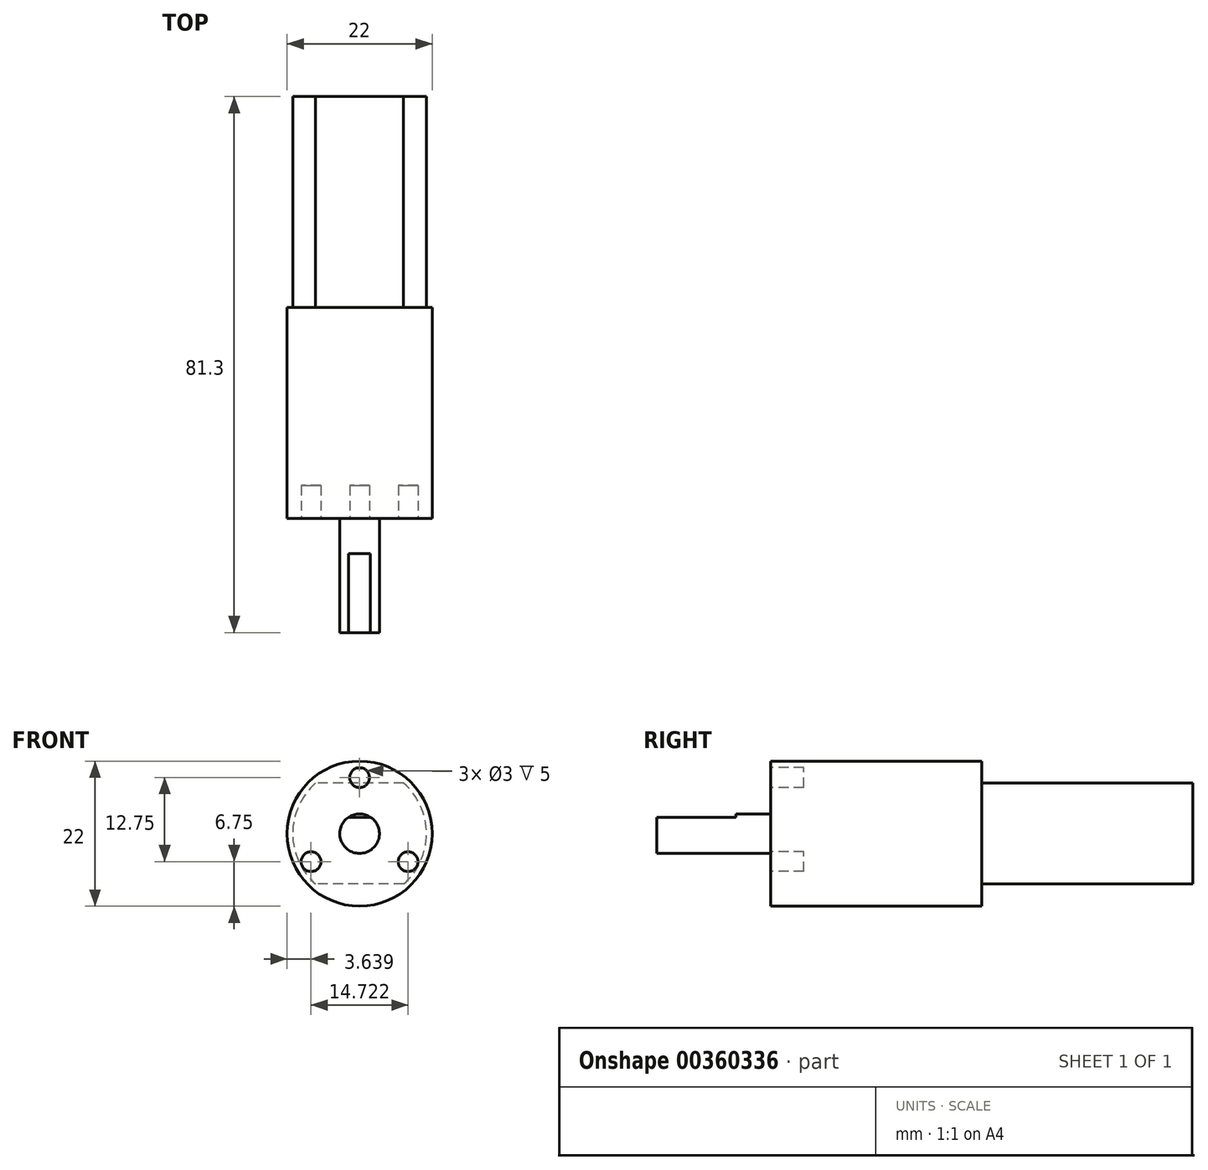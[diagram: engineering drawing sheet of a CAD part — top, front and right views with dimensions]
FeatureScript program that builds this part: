
annotation { "Feature Type Name" : "Feature", "Feature Type Description" : "" }
export const myFeature = defineFeature(function(context is Context, id is Id, definition is map)
    precondition{}
    {
        {
            var Q0;
            Q0=qCreatedBy(makeId("Front.planeOp"),FACE);
            var sketch = newSketch(context, id + "F0", { "sketchPlane" : qUnion([Q0])});
            skCircle(sketch, "E0", {"center": v(0, 0) * mm, "radius": 11 * mm});
            skSolve(sketch);
        }
        {
            var Q0;
            Q0 = qSketchRegion(id + "F0", true);
            extrude(context, id + "F1", {"entities" : qUnion([Q0]), "depth" : 32 * mm});
        }
        {
            var Q0;
            Q0=makeQuery(id+"F1.opExtrude","CAP_FACE",FACE,{"disambiguationData":[OSD([sQuery(id+"F0.wireOp",EDGE,"E0")])],"isStart":false});
            var sketch = newSketch(context, id + "F2", { "sketchPlane" : qUnion([Q0])});
            skCircle(sketch, "E1", {"center": v(0, 8.5) * mm, "radius": 1.5 * mm});
            skCircle(sketch, "E2.1.0", {"center": v(-7.36, -4.25) * mm, "radius": 1.5 * mm});
            skCircle(sketch, "E2.2.0", {"center": v(7.36, -4.25) * mm, "radius": 1.5 * mm});
            skPoint(sketch, "E2.center", {"position": v(0, 0) * mm});
            skSolve(sketch);
        }
        {
            var Q0;
            Q0 = qSketchRegion(id + "F2", true);
            extrude(context, id + "F3", {"entities" : qUnion([Q0]), "operationType" : NewBodyOperationType.REMOVE, "oppositeDirection" : true, "depth" : 5 * mm});
        }
        {
            var Q0;
            Q0=makeQuery(id+"F1.opExtrude","CAP_FACE",FACE,{"disambiguationData":[OSD([sQuery(id+"F0.wireOp",EDGE,"E0")])],"isStart":true});
            var sketch = newSketch(context, id + "F4", { "sketchPlane" : qUnion([Q0])});
            skArc(sketch, "E3", {"start": v(-6.67, 7.65) * mm, "mid": v(-10.15, 0) * mm, "end": v(-6.67, -7.65) * mm});
            skArc(sketch, "E4", {"start": v(6.67, 7.65) * mm, "mid": v(10.15, 0) * mm, "end": v(6.67, -7.65) * mm});
            skLineSegment(sketch, "E5", {"start": v(-6.67, -7.65) * mm, "end": v(6.67, -7.65) * mm});
            skLineSegment(sketch, "E6", {"start": v(-6.67, 7.65) * mm, "end": v(6.67, 7.65) * mm});
            skLineSegment(sketch, "E7", {"start": v(0, 7.65) * mm, "end": v(0, -7.65) * mm, "construction": true});
            skSolve(sketch);
        }
        {
            var Q0;
            Q0 = qSketchRegion(id + "F4", true);
            extrude(context, id + "F5", {"entities" : qUnion([Q0]), "operationType" : NewBodyOperationType.ADD, "depth" : 32 * mm});
        }
        {
            var Q0;
            Q0=makeQuery(id+"F1.opExtrude","CAP_FACE",FACE,{"disambiguationData":[OSD([sQuery(id+"F0.wireOp",EDGE,"E0")])],"isStart":false});
            var sketch = newSketch(context, id + "F6", { "sketchPlane" : qUnion([Q0])});
            skCircle(sketch, "E8", {"center": v(0, 0) * mm, "radius": 3 * mm});
            skSolve(sketch);
        }
        {
            var Q0;
            Q0 = qSketchRegion(id + "F6", true);
            extrude(context, id + "F7", {"entities" : qUnion([Q0]), "operationType" : NewBodyOperationType.ADD, "depth" : 17.3 * mm});
        }
        {
            var Q0;
            Q0=makeQuery(id+"F7.opExtrude","CAP_FACE",FACE,{"disambiguationData":[OSD([sQuery(id+"F6.wireOp",EDGE,"E8")])],"isStart":false});
            var sketch = newSketch(context, id + "F8", { "sketchPlane" : qUnion([Q0])});
            skLineSegment(sketch, "E9", {"start": v(-1.66, 2.5) * mm, "end": v(1.66, 2.5) * mm});
            skArc(sketch, "E10", {"start": v(-1.66, 2.5) * mm, "mid": v(0, 3) * mm, "end": v(1.66, 2.5) * mm});
            skSolve(sketch);
        }
        {
            var Q0;
            Q0 = qSketchRegion(id + "F8", true);
            extrude(context, id + "F9", {"entities" : qUnion([Q0]), "operationType" : NewBodyOperationType.REMOVE, "oppositeDirection" : true, "depth" : 12 * mm});
        }
    });
